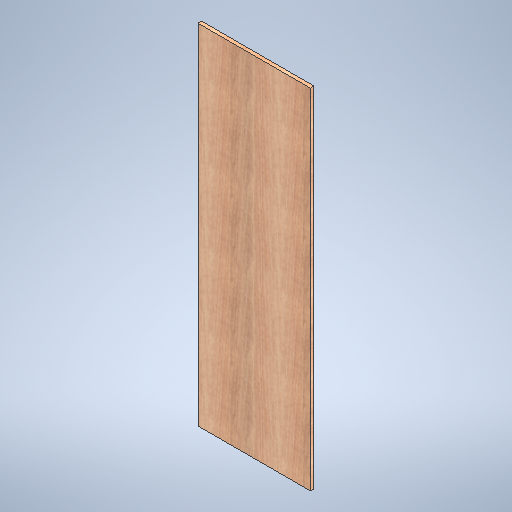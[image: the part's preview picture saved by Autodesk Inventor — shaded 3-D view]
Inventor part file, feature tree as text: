
AUTODESK INVENTOR PART (.ipt)
format: ipt  version: 2025.1 (Build 291241020, 241B)  size: 373,248 bytes
history: native  units: in
note: dims shown in document units (in); Inventor stores cm internally (conversion verified against a paired STEP export)
features: extrude x1, sketch x1
ambient origin geometry x8: Origin, YZ Plane, XZ Plane, XY Plane, X Axis, Y Axis, Z Axis, Center Point
bodies: Solid1 (feature_tree)
feature tree (2):
  extrude  "Extrusion1"  Depth=15.459in
  sketch  "Sketch1"  dims[d2=48.0in d3=15.459in d4=0.5in d5=0.0in]
